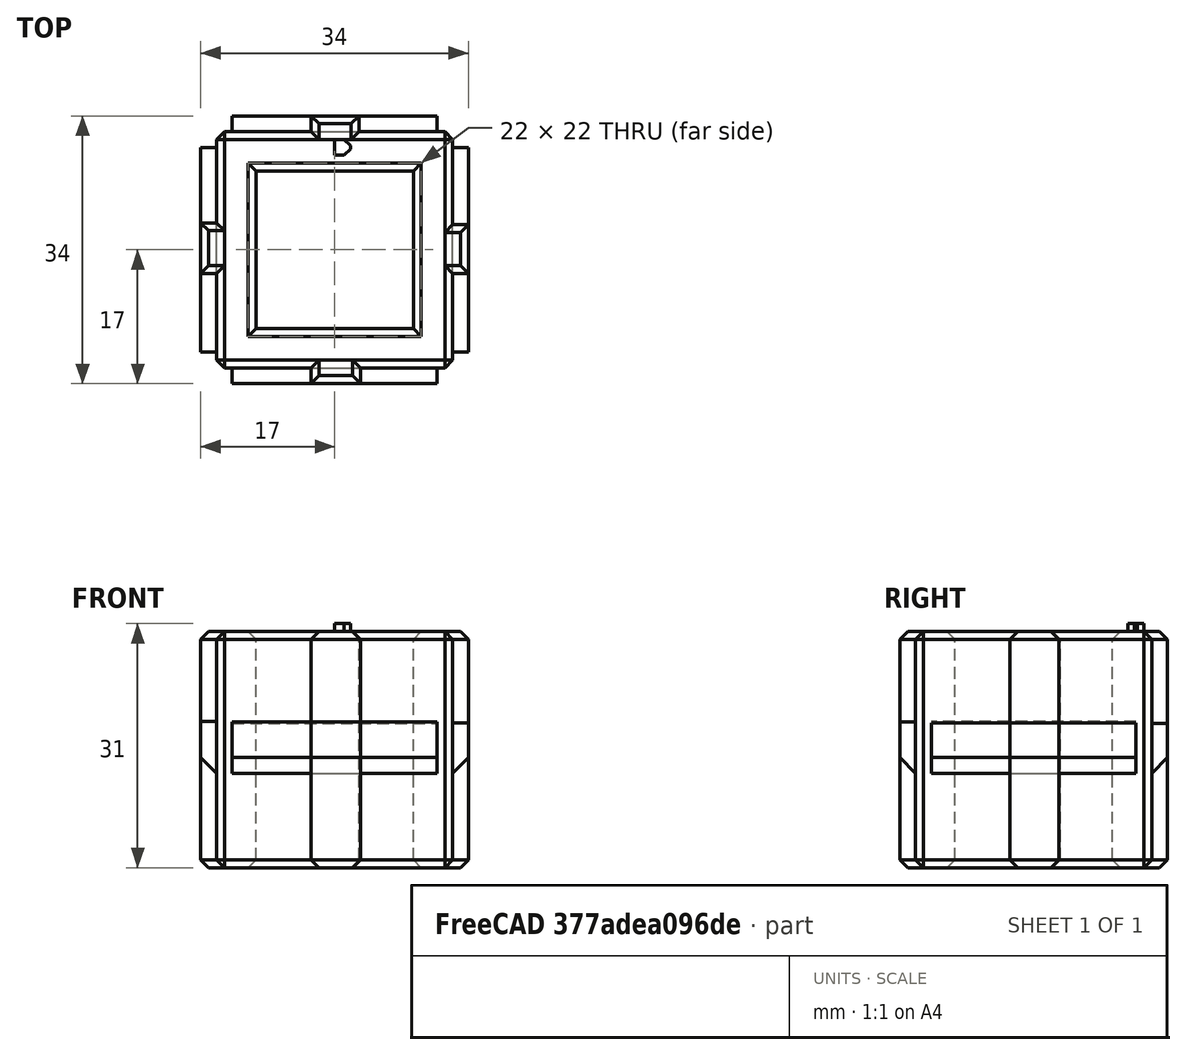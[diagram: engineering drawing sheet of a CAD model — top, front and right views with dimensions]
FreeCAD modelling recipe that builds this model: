
FCSTD DOCUMENT  (FreeCAD 0.18R16146 (Git))
Label: 3030-aligner-test
License: All rights reserved
LicenseURL: http://en.wikipedia.org/wiki/All_rights_reserved
objects: Part::Chamfer×13, Part::Box×11, Part::MultiFuse×2, Part::Feature×2, Part::Cut×1
note: 29 computed .brp shape members not serialized (recipe doc carries the construction recipe); baked Part::Feature solids carry a one-line shape summary decoded from their .brp

FEATURE [Part::Box] Box  label="Cube"
  AttacherType = Attacher::AttachEngine3D
  Height = 30
  Length = 30
  Placement = pos=(-15,-15,0) rot=(0,0,1;0rad)
  Width = 30
FEATURE [Part::Box] Box001  label="Cube001"
  AttacherType = Attacher::AttachEngine3D
  Height = 30
  Length = 20
  Placement = pos=(-10,-10,0) rot=(0,0,1;0rad)
  Width = 20
FEATURE [Part::Cut] Cut
  Base = -> Box
  Tool = -> Box001
FEATURE [Part::Box] Box002  label="Cube002"
  AttacherType = Attacher::AttachEngine3D
  Height = 6.4
  Length = 3
  Placement = pos=(14,-13,12) rot=(0,0,1;0rad)
  Width = 26
FEATURE [Part::Box] Box003  label="Cube003"
  AttacherType = Attacher::AttachEngine3D
  Height = 6.6
  Length = 3
  Placement = pos=(-17,-13,12) rot=(0,0,1;0rad)
  Width = 26
FEATURE [Part::Box] Box004  label="Cube004"
  AttacherType = Attacher::AttachEngine3D
  Height = 6.3
  Length = 26
  Placement = pos=(-13,14,12) rot=(0,0,1;0rad)
  Width = 3
FEATURE [Part::Box] Box005  label="Cube005"
  AttacherType = Attacher::AttachEngine3D
  Height = 6.5
  Length = 26
  Placement = pos=(-13,-17,12) rot=(0,0,1;0rad)
  Width = 3
FEATURE [Part::Box] Box006  label="Cube006"
  AttacherType = Attacher::AttachEngine3D
  Height = 2
  Length = 2
  Placement = pos=(0,12,29) rot=(0,0,1;0rad)
  Width = 2
FEATURE [Part::Chamfer] Chamfer
  Base = -> Box006
  Edges = 2 edges r=0.8: [Edge5,Edge7]
FEATURE [Part::Chamfer] Chamfer001
  Base = -> Box004
  Edges = 1 edges r=2: [Edge11]
FEATURE [Part::Chamfer] Chamfer002
  Base = -> Box003
  Edges = 1 edges r=2: [Edge4]
FEATURE [Part::Chamfer] Chamfer003
  Base = -> Box005
  Edges = 1 edges r=2: [Edge9]
FEATURE [Part::Chamfer] Chamfer004
  Base = -> Box002
  Edges = 1 edges r=2: [Edge8]
FEATURE [Part::Chamfer] Chamfer005
  Base = -> Cut
  Edges = 20 edges r=1: [Edge1,Edge2,Edge3,Edge4,Edge5,Edge6,Edge7,Edge8,Edge9,Edge10,Edge11,Edge12,Edge13,Edge14,Edge15,Edge16,Edge17,Edge18,Edge19,Edge20]
FEATURE [Part::MultiFuse] Fusion
  Shapes = -> [Chamfer005,Chamfer002,Chamfer004,Chamfer003,Chamfer001,Chamfer]
FEATURE [Part::Feature] Chamfer005001  label="Chamfer006"
  shape: bbox 30 x 30 x 30 mm, 38 faces (baked)
FEATURE [Part::Box] Box007  label="Cube007"
  AttacherType = Attacher::AttachEngine3D
  Height = 30
  Length = 6.1
  Placement = pos=(-3,11,0) rot=(0,0,1;0rad)
  Width = 6
FEATURE [Part::Box] Box008  label="Cube008"
  AttacherType = Attacher::AttachEngine3D
  Height = 30
  Length = 6
  Placement = pos=(11,-3,0) rot=(0,0,1;0rad)
  Width = 6.2
FEATURE [Part::Box] Box009  label="Cube009"
  AttacherType = Attacher::AttachEngine3D
  Height = 30
  Length = 6.3
  Placement = pos=(-3,-17,0) rot=(0,0,1;0rad)
  Width = 6
FEATURE [Part::Box] Box010  label="Cube010"
  AttacherType = Attacher::AttachEngine3D
  Height = 30
  Length = 6
  Placement = pos=(-17,-3,0) rot=(0,0,1;0rad)
  Width = 6.4
FEATURE [Part::Feature] Chamfer005002  label="Chamfer007"
  shape: bbox 2 x 2 x 2 mm, 8 faces (baked)
FEATURE [Part::Chamfer] Chamfer005003
  Base = -> Box010
  Edges = 3 edges r=1: [Edge4,Edge9,Edge11]
FEATURE [Part::Chamfer] Chamfer005004
  Base = -> Box009
  Edges = 3 edges r=1: [Edge4,Edge8,Edge9]
FEATURE [Part::Chamfer] Chamfer005005
  Base = -> Box008
  Edges = 3 edges r=1: [Edge8,Edge9,Edge11]
FEATURE [Part::Chamfer] Chamfer005006
  Base = -> Box007
  Edges = 6 edges r=1: [Edge2,Edge4,Edge6,Edge8,Edge11,Edge12]
FEATURE [Part::Chamfer] Chamfer005007
  Base = -> Chamfer005005
  Edges = 3 edges r=1: [Edge9,Edge12,Edge13]
FEATURE [Part::Chamfer] Chamfer005008
  Base = -> Chamfer005004
  Edges = 3 edges r=1: [Edge3,Edge7,Edge12]
FEATURE [Part::Chamfer] Chamfer005009
  Base = -> Chamfer005003
  Edges = 3 edges r=1: [Edge3,Edge7,Edge11]
FEATURE [Part::MultiFuse] Fusion001
  Shapes = -> [Chamfer005009,Chamfer005008,Chamfer005007,Chamfer005006,Chamfer005002,Chamfer005001]
